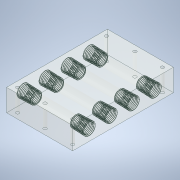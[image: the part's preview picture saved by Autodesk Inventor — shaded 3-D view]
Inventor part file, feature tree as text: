
AUTODESK INVENTOR PART (.ipt)
format: ipt  version: 2020 (Build 240168000, 168)  size: 7,270,912 bytes
history: native  units: mm
features: sketch x30, revolve x16, thread x8, helix x8, extrude x6
ambient origin geometry x8: Origin, YZ Plane, XZ Plane, XY Plane, X Axis, Y Axis, Z Axis, Center Point
bodies: Solid1 (feature_tree), Solid2 (feature_tree), Solid3 (feature_tree), Solid4 (feature_tree), Solid5 (feature_tree), Solid10 (feature_tree), Solid11 (feature_tree), Solid12 (feature_tree), Solid13 (feature_tree)
feature tree (68):
  extrude  "Extrusion1"  Depth=76.2mm
  extrude  "Extrusion2"  Depth=19.05mm
  extrude  "Extrusion3"  Depth=80.0mm
  extrude  "Extrusion4"  Depth=19.05mm
  extrude  "Extrusion5"  Depth=80.0mm
  thread  "Thread13"  [1 undecoded]
  thread  "Thread14"  [1 undecoded]
  thread  "Thread15"  [1 undecoded]
  thread  "Thread16"  [1 undecoded]
  thread  "Thread21"  [1 undecoded]
  thread  "Thread22"  [1 undecoded]
  thread  "Thread23"  [1 undecoded]
  thread  "Thread24"  [1 undecoded]
  revolve  "Revolution1"  [1 undecoded]
  revolve  "Revolution2"  [1 undecoded]
  helix  "Coil1"  [1 undecoded]
  revolve  "Revolution3"  [1 undecoded]
  revolve  "Revolution4"  [1 undecoded]
  helix  "Coil2"  [1 undecoded]
  revolve  "Revolution5"  [1 undecoded]
  revolve  "Revolution6"  [1 undecoded]
  helix  "Coil3"  [1 undecoded]
  revolve  "Revolution7"  [1 undecoded]
  revolve  "Revolution8"  [1 undecoded]
  helix  "Coil4"  [1 undecoded]
  revolve  "Revolution17"  [1 undecoded]
  revolve  "Revolution18"  [1 undecoded]
  helix  "Coil9"  [1 undecoded]
  revolve  "Revolution19"  [1 undecoded]
  revolve  "Revolution20"  [1 undecoded]
  helix  "Coil10"  [1 undecoded]
  revolve  "Revolution21"  [1 undecoded]
  revolve  "Revolution22"  [1 undecoded]
  helix  "Coil11"  [1 undecoded]
  revolve  "Revolution23"  [1 undecoded]
  revolve  "Revolution24"  [1 undecoded]
  helix  "Coil12"  [1 undecoded]
  extrude  "Extrusion6"  Depth=1.412522mm
  sketch  "Sketch1"  dims[d0=215.9mm d1=76.2mm]
  sketch  "Sketch2"  dims[d2=25.4mm d3=0.0mm d4=19.05mm]
  sketch  "Sketch3"  dims[d5=9.8mm d6=80.0mm d8=25.4mm d9=10.0mm d11=10.0mm]
  sketch  "Sketch4"  dims[d13=63.5mm d14=0.0mm d15=19.05mm]
  sketch  "Sketch5"  dims[d16=12.2mm d17=80.0mm d19=25.4mm d20=10.0mm d22=10.0mm d24=16.0mm d25=-0.312414mm d36=6.35mm d37=3.8mm d40=0.0mm d41=0.0mm d42=6.35mm d43=30.0mm d45=100.6mm d46=30.0mm d48=31.75mm]
  sketch  "Sketch6"  dims[d68=80.0mm d70=10.0mm d71=19.05mm d72=12.2mm d73=25.4mm d74=10.0mm d75=16.0mm d76=-0.312414mm d77=15.103mm d78=0.0mm d79=15.103mm d80=0.0mm]
  sketch  "Sketch7"  dims[d81=15.103mm d82=0.0mm d83=15.103mm d84=0.0mm]
  sketch  "Sketch8"  dims[d93=15.103mm d94=0.0mm d95=15.103mm d96=0.0mm d97=15.103mm d98=0.0mm]
  sketch  "Sketch9"  dims[d99=15.103mm d100=0.0mm d109=9.599311mm d110=0.225895mm d111=0.225895mm]
  sketch  "Sketch10"  dims[d114=1.411111mm d116=9.599311mm d118=0.0mm]
  sketch  "Sketch11"  dims[d119=0.0mm]
  sketch  "Sketch12"  dims[d120=1.412522mm d121=17.925222mm d122=10.0mm d123=-0.312414mm d124=0.0mm d125=0.0mm d126=0.0mm d127=0.0mm d128=9.599311mm d129=0.225895mm d130=0.225895mm]
  sketch  "Sketch13"  dims[d133=1.411111mm d135=9.599311mm d137=0.0mm]
  sketch  "Sketch14"  dims[d138=0.0mm]
  sketch  "Sketch15"  dims[d139=1.412522mm d140=17.925222mm d141=10.0mm d142=-0.312414mm d143=0.0mm d144=0.0mm d145=0.0mm d146=0.0mm d147=9.599311mm d148=0.225895mm d149=0.225895mm]
  sketch  "Sketch16"  dims[d152=1.411111mm d154=9.599311mm d156=0.0mm]
  sketch  "Sketch17"  dims[d157=0.0mm]
  sketch  "Sketch30"  dims[d158=1.412522mm d159=17.925222mm d160=10.0mm d161=-0.312414mm d162=0.0mm d163=0.0mm d164=0.0mm d165=0.0mm d166=9.599311mm d167=0.225895mm d168=0.225895mm]
  sketch  "Sketch31"  dims[d171=1.411111mm d173=9.599311mm d175=0.0mm]
  sketch  "Sketch32"  dims[d176=0.0mm]
  sketch  "Sketch33"  dims[d177=1.412522mm d178=17.925222mm d179=10.0mm d180=-0.312414mm d181=0.0mm d182=0.0mm d183=0.0mm d184=0.0mm d192=9.599311mm]
  sketch  "Sketch34"  dims[d211=9.599311mm d230=9.599311mm d249=9.599311mm]
  sketch  "Sketch35"  dims[d261=9.599311mm d262=0.225895mm d263=0.225895mm d266=1.411111mm]
  sketch  "Sketch36"  dims[d268=9.599311mm d270=0.0mm d271=0.0mm]
  sketch  "Sketch37"  dims[d272=1.412522mm d273=17.925222mm d274=10.0mm d275=-0.312414mm d276=0.0mm d277=0.0mm d278=0.0mm d279=0.0mm d280=9.599311mm d281=0.225895mm d282=0.225895mm]
  sketch  "Sketch38"  dims[d285=1.411111mm d287=9.599311mm d289=0.0mm]
  sketch  "Sketch39"  dims[d290=0.0mm]
  sketch  "Sketch40"  dims[d291=1.412522mm d292=17.925222mm d293=10.0mm d294=-0.312414mm d295=0.0mm d296=0.0mm d297=0.0mm d298=0.0mm d299=9.599311mm d300=0.225895mm d301=0.225895mm]
  sketch  "Sketch41"  dims[d304=1.411111mm]
  sketch  "Sketch56"  dims[d306=9.599311mm d308=0.0mm d309=0.0mm d310=1.412522mm d311=17.925222mm d312=10.0mm d313=-0.312414mm d314=0.0mm d315=0.0mm d316=0.0mm d317=0.0mm d318=9.599311mm d319=0.225895mm d320=0.225895mm d323=1.411111mm d325=9.599311mm d327=0.0mm d328=0.0mm d329=1.412522mm d330=17.925222mm d331=10.0mm d332=-0.312414mm d333=0.0mm d334=0.0mm d335=0.0mm d336=0.0mm d344=9.599311mm d363=9.599311mm d382=9.599311mm d401=9.599311mm d413=6.35mm d414=0.0mm d415=0.0mm d416=2.0mm]
note: 32 required parameter values undecoded (feature->parameter linkage not recoverable at this tier; creation-order binding heuristic only, values carry confidence <= 0.55)